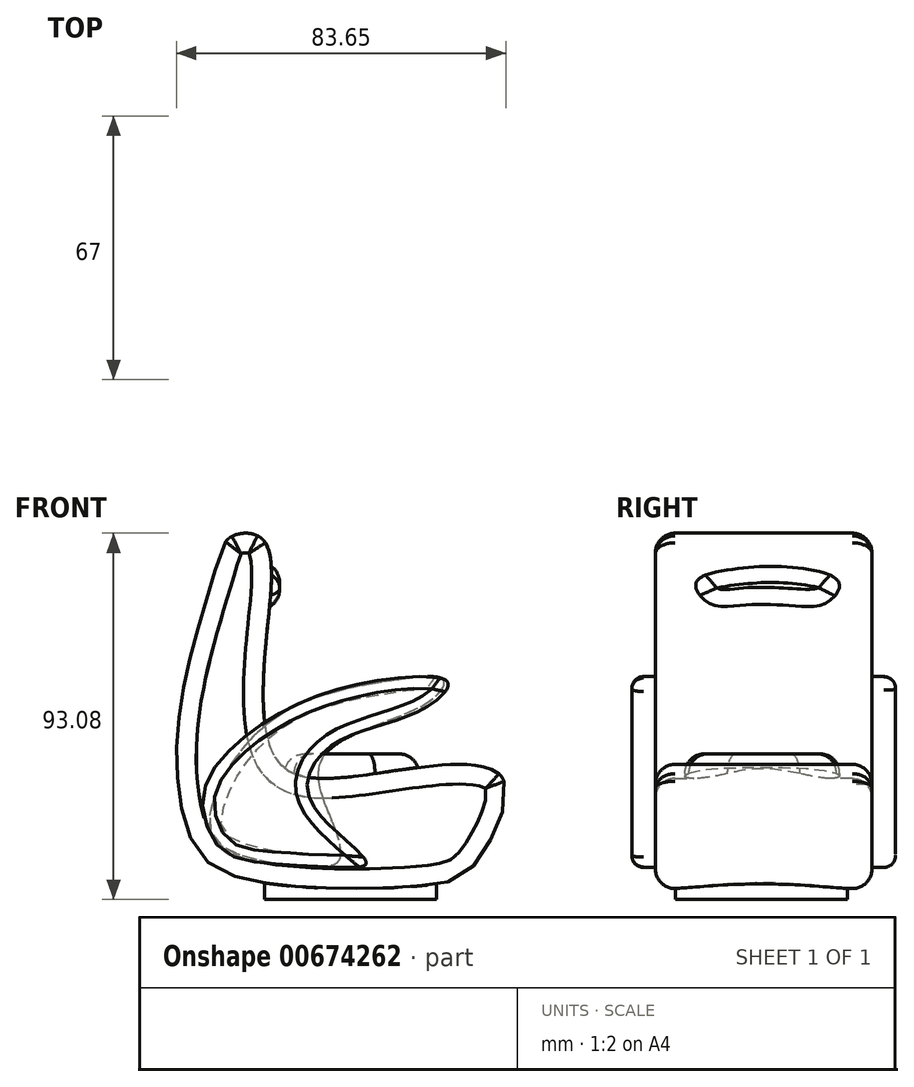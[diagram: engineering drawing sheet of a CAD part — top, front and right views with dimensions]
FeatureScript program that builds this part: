
annotation { "Feature Type Name" : "Feature", "Feature Type Description" : "" }
export const myFeature = defineFeature(function(context is Context, id is Id, definition is map)
    precondition{}
    {
        {
            var Q0;
            Q0=qCreatedBy(makeId("Front.planeOp"),FACE);
            var sketch = newSketch(context, id + "F0", { "sketchPlane" : qUnion([Q0])});
            skFitSpline(sketch, "E0", {"points": [v(-34.23, 32.24) * mm, v(-43.49, -5.13) * mm, v(-40.51, -36.54) * mm, v(-26.95, -46.8) * mm, v(21.33, -48.12) * mm, v(32.24, -42.17) * mm, v(38.53, -21) * mm, v(3.8, -20.34) * mm, v(-18.35, -17.03) * mm, v(-21.33, 14.72) * mm, v(-22.32, 39.52) * mm, v(-30.26, 40.18) * mm, v(-34.23, 32.24) * mm]});
            skSolve(sketch);
        }
        {
            var Q0;
            Q0 = qSketchRegion(id + "F0", true);
            extrude(context, id + "F1", {"entities" : qUnion([Q0]), "depth" : 55 * mm, "offsetDistance" : 25 * mm});
        }
        {
            var Q0;
            Q0=makeQuery(id+"F1.opExtrude","CAP_EDGE",EDGE,{"disambiguationData":[OSD([sQuery(id+"F0.wireOp",EDGE,"E0")])],"isStart":true});
            fillet(context, id + "F2", {"entities" : qUnion([Q0]), "radius" : 5 * mm, "tangentPropagation" : true, "allowEdgeOverflow" : false});
        }
        {
            var Q0;
            Q0=makeQuery(id+"F1.opExtrude","CAP_EDGE",EDGE,{"disambiguationData":[OSD([sQuery(id+"F0.wireOp",EDGE,"E0")])],"isStart":false});
            fillet(context, id + "F3", {"entities" : qUnion([Q0]), "radius" : 5 * mm, "tangentPropagation" : true, "allowEdgeOverflow" : false});
        }
        {
            var Q0;
            Q0=qCreatedBy(makeId("Top.planeOp"),FACE);
            cPlane(context, id + "F4", {"entities" : qUnion([Q0]), "cplaneType" : CPlaneType.OFFSET, "offset" : 25 * mm, "oppositeDirection" : true, "width" : 150 * mm, "height" : 150 * mm});
        }
        {
            var Q0;
            Q0=qCreatedBy(id+"F4.planeOp",FACE);
            var sketch = newSketch(context, id + "F5", { "sketchPlane" : qUnion([Q0])});
            skFitSpline(sketch, "E1", {"points": [v(0, -8.35) * mm, v(-11.63, -14.37) * mm, v(-16.56, -28.33) * mm, v(-12.18, -40.1) * mm, v(0, -47.49) * mm, v(14.1, -41.2) * mm, v(17.1, -28.88) * mm, v(15.46, -16.83) * mm, v(7.8, -9.72) * mm, v(0, -8.35) * mm]});
            skSolve(sketch);
        }
        {
            var Q0;
            Q0 = qSketchRegion(id + "F5", true);
            extrude(context, id + "F6", {"entities" : qUnion([Q0]), "operationType" : NewBodyOperationType.ADD, "depth" : 10 * mm, "offsetDistance" : 25 * mm});
        }
        {
            var Q0;
            Q0=makeQuery(id+"F6.opExtrude","CAP_EDGE",EDGE,{"disambiguationData":[OSD([sQuery(id+"F5.wireOp",EDGE,"E1")])],"isStart":false});
            fillet(context, id + "F7", {"entities" : qUnion([Q0]), "radius" : 5 * mm, "tangentPropagation" : true, "allowEdgeOverflow" : false});
        }
        {
            var Q0;
            Q0=qCreatedBy(makeId("Right.planeOp"),FACE);
            cPlane(context, id + "F8", {"entities" : qUnion([Q0]), "cplaneType" : CPlaneType.OFFSET, "offset" : 25 * mm, "oppositeDirection" : true, "width" : 150 * mm, "height" : 150 * mm});
        }
        {
            var Q0;
            Q0=qCreatedBy(id+"F8.planeOp",FACE);
            var sketch = newSketch(context, id + "F9", { "sketchPlane" : qUnion([Q0])});
            skFitSpline(sketch, "E2", {"points": [v(-44.66, 28.5) * mm, v(-34.26, 32.07) * mm, v(-19.7, 32.37) * mm, v(-8.4, 28.5) * mm, v(-11.38, 23.45) * mm, v(-19.1, 22.56) * mm, v(-31.88, 22.86) * mm, v(-41.1, 23.15) * mm, v(-44.66, 28.5) * mm]});
            skSolve(sketch);
        }
        {
            var Q0;
            Q0 = qSketchRegion(id + "F9", true);
            extrude(context, id + "F10", {"entities" : qUnion([Q0]), "operationType" : NewBodyOperationType.ADD, "depth" : 7 * mm, "offsetDistance" : 25 * mm});
        }
        {
            var Q0;
            Q0=makeQuery(id+"F10.opExtrude","CAP_EDGE",EDGE,{"disambiguationData":[OSD([sQuery(id+"F9.wireOp",EDGE,"E2")])],"isStart":false});
            fillet(context, id + "F11", {"entities" : qUnion([Q0]), "radius" : 5 * mm, "tangentPropagation" : true, "allowEdgeOverflow" : false});
        }
        {
            var Q0;
            Q0=qCreatedBy(makeId("Front.planeOp"),FACE);
            var sketch = newSketch(context, id + "F12", { "sketchPlane" : qUnion([Q0])});
            skFitSpline(sketch, "E3", {"points": [v(13.52, 4.01) * mm, v(-15, -3.42) * mm, v(-31.65, -19.76) * mm, v(-35.8, -33.43) * mm, v(-31.65, -39.08) * mm, v(-18.28, -42.94) * mm, v(-9.66, -43.83) * mm, v(-3.12, -42.35) * mm, v(-4.01, -33.73) * mm, v(-6.98, -15.9) * mm, v(19.17, -2.23) * mm, v(23.62, 3.71) * mm, v(13.52, 4.01) * mm]});
            skSolve(sketch);
        }
        {
            var Q0;
            Q0 = qSketchRegion(id + "F12", true);
            extrude(context, id + "F13", {"entities" : qUnion([Q0]), "operationType" : NewBodyOperationType.ADD, "oppositeDirection" : true, "depth" : 6 * mm, "offsetDistance" : 25 * mm});
        }
        {
            var Q0;
            Q0=makeQuery(id+"F13.opExtrude","CAP_EDGE",EDGE,{"disambiguationData":[OSD([sQuery(id+"F12.wireOp",EDGE,"E3")])],"isStart":false});
            fillet(context, id + "F14", {"entities" : qUnion([Q0]), "radius" : 3 * mm, "tangentPropagation" : true, "allowEdgeOverflow" : false});
        }
        {
            var Q0;
            Q0=qCreatedBy(makeId("Front.planeOp"),FACE);
            cPlane(context, id + "F15", {"entities" : qUnion([Q0]), "cplaneType" : CPlaneType.OFFSET, "offset" : 55 * mm, "width" : 150 * mm, "height" : 150 * mm});
        }
        {
            var Q0;
            Q0=qCreatedBy(id+"F15.planeOp",FACE);
            var sketch = newSketch(context, id + "F16", { "sketchPlane" : qUnion([Q0])});
            skFitSpline(sketch, "E4", {"points": [v(20.06, 4.6) * mm, v(-7.58, 0) * mm, v(-31.05, -14.41) * mm, v(-37.6, -26.9) * mm, v(-32.54, -39.37) * mm, v(-18.87, -42.94) * mm, v(0, -43.83) * mm, v(4.01, -42.64) * mm, v(-6.98, -31.35) * mm, v(-10.85, -21.54) * mm, v(-3.42, -12.04) * mm, v(18.28, -3.71) * mm, v(24.81, 2.82) * mm, v(20.06, 4.6) * mm]});
            skSolve(sketch);
        }
        {
            var Q0;
            Q0 = qSketchRegion(id + "F16", true);
            extrude(context, id + "F17", {"entities" : qUnion([Q0]), "operationType" : NewBodyOperationType.ADD, "depth" : 6 * mm, "offsetDistance" : 25 * mm});
        }
        {
            var Q0;
            Q0=makeQuery(id+"F17.opExtrude","CAP_EDGE",EDGE,{"disambiguationData":[OSD([sQuery(id+"F16.wireOp",EDGE,"E4")])],"isStart":false});
            fillet(context, id + "F18", {"entities" : qUnion([Q0]), "radius" : 3 * mm, "tangentPropagation" : true, "allowEdgeOverflow" : false});
        }
        {
            var Q0;
            Q0=qCreatedBy(id+"F4.planeOp",FACE);
            var sketch = newSketch(context, id + "F19", { "sketchPlane" : qUnion([Q0])});
            skCircle(sketch, "E5", {"center": v(0, -28.08) * mm, "radius": 21.85 * mm});
            skSolve(sketch);
        }
        {
            var Q0;
            Q0 = qSketchRegion(id + "F19", true);
            extrude(context, id + "F20", {"entities" : qUnion([Q0]), "operationType" : NewBodyOperationType.ADD, "oppositeDirection" : true, "depth" : 27 * mm, "offsetDistance" : 25 * mm});
        }
    });
